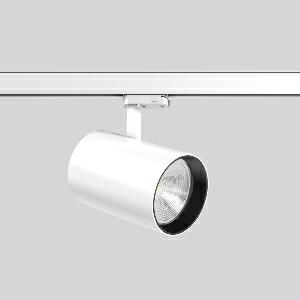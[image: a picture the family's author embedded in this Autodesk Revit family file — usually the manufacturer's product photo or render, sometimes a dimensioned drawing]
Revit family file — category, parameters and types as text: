
# Revit family: deecos_s_maxi_742224_002_3_bcde
name_source: partatom
category: Lighting Fixtures
units: mm (PartAtom-declared; Revit-internal decimal feet)

## family parameters
Cut with Voids When Loaded = No
Host = Face
Light Source = No
Part Type = Normal
Room Calculation Point = No
Round Connector Dimension = Use Diameter
Shared = No

## types (1)
- DEECOS S maxi (1 x LED Modul 935, 3750 lm, 3500)
    Apparent Load = 35 VA
    Approval mark = CE
    CIE Flux Codes = 97 100 100 100 100
    Color Rendering = 92
    Color Temperature = 3500
    Default Elevation = 1800 mm
    Description = Series: DEECOS S maxi
LED surface-mounted projector in modern design with no visible cooling ribs. Housing: die-cast aluminium, powder-coated. Rotation range: 356°. Swivel range: 90°. Black plastic ring and recessed LED to prevent glare from the side. Optical assembly with lens made of plastic (polycarbonate) for the best homogeneous light distribution - can be changed without tools. Best colour rendering index Ra>90. With multi adaptor for 3-circuit tracks 230 V. Suitable for Track on ceiling, Wall track. High quality converter without flickering and stroboscopic effect. The following accessories can be mounted without use of tools: interchangeable lenses, decorative glasses, honeycomb louvre, clear and frosted diffusers, white interchangeable plastic ring. 
Colour: traffic white, matt (RAL 9016)
Diameter: 123 mm
Height: 200 mm
Lamp: LED
Socket: without socket
Colour temperature: 3500K
Colour rendering index (CRI): 92
System power: 35 W
Rated luminous flux: 3750 lm
Luminous efficiency: 107 lm/W
Control gear: Regulated power supply
Protection class: I
Type of protection: IP 20
    Height = 200 mm  [stored 0.656168 ft]
    Lamp = 1 x LED Modul 935
    Lamp Light Flux = 3750 lm
    Lamp count = 1
    Length = 123 mm
    Lifetime = 50000 h
    Luminous efficacy = 107 lm/W
    Manufacturer = RZB
    ModVariant = No
    Model = 742224.002.3
    Mounting Place = Ceiling
    Mounting Type = Rail mounted
    Number of Poles = 1
    OnlyDefault = Yes
    Power Factor = 1
    Product Name = DEECOS S maxi
    Product group = Track mounted projectors
    ProductGroupID = 301
    Protection Class = Protection class I
    Protection Degree = IP 20
    RLX_Detail_Level = 1
    RLX_Emergency_Light_Flux = 0 lm
    RLX_Emergency_Type = 0
    RLX_Emergency_Type_DB = No
    RlxData = <blob elided: 39281 chars, md5=ac5c671f>
    Socket = socket
    Standby Power = 0 W
    System Light Flux = 3750 lm
    System Power = 35 W
    Type Comments = Product without accessories
    Type Image = 741958.002.jpg
    URL = http://relux.com
    VarID = ---
    Voltage = 230 V
    Voltage Range = 220-240 V
    Weight = 0.00 kg
    Width = 0 mm  [stored 0 ft]

note: [stored X ft] marks values corroborated as IEEE doubles in the binary element streams (Revit-internal decimal feet)

## geometry (parser evidence)
native form markers: Blend x4, Sweep x12
no freeform markers — native parametric forms only
